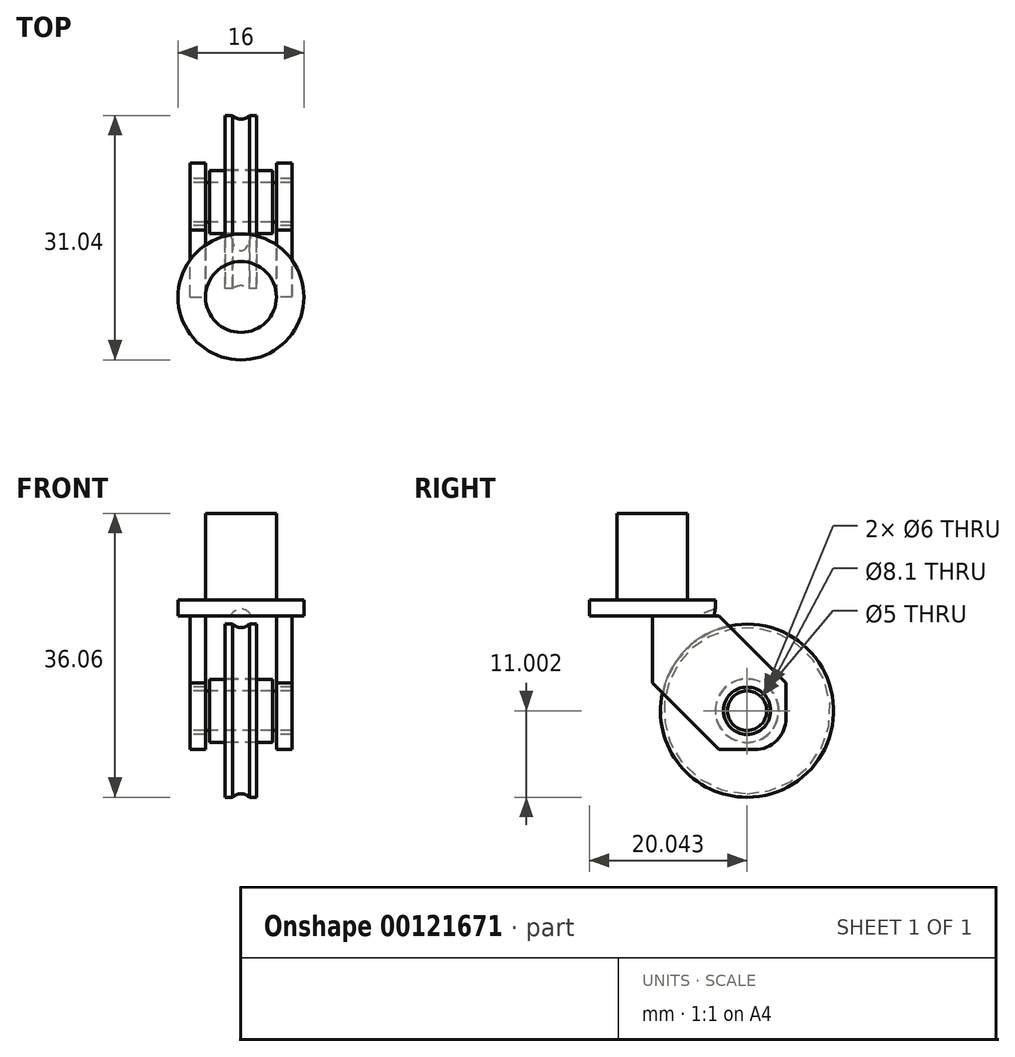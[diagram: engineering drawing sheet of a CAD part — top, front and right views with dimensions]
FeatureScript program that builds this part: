
annotation { "Feature Type Name" : "Feature", "Feature Type Description" : "" }
export const myFeature = defineFeature(function(context is Context, id is Id, definition is map)
    precondition{}
    {
        {
            var Q0;
            Q0=qCreatedBy(makeId("Top.planeOp"),FACE);
            var sketch = newSketch(context, id + "F0", { "sketchPlane" : qUnion([Q0])});
            skCircle(sketch, "E0", {"center": v(0, 0) * mm, "radius": 4.5 * mm});
            skCircle(sketch, "E1", {"center": v(0, 0) * mm, "radius": 8 * mm});
            skLineSegment(sketch, "E2.bottom", {"start": v(-6.5, 0) * mm, "end": v(-4.5, 0) * mm});
            skLineSegment(sketch, "E2.top", {"start": v(-6.5, 17) * mm, "end": v(-4.5, 17) * mm});
            skLineSegment(sketch, "E2.left", {"start": v(-6.5, 0) * mm, "end": v(-6.5, 17) * mm});
            skLineSegment(sketch, "E2.right", {"start": v(-4.5, 0) * mm, "end": v(-4.5, 17) * mm});
            skLineSegment(sketch, "E3.MirrorCS", {"start": v(6.5, 17) * mm, "end": v(4.5, 17) * mm});
            skLineSegment(sketch, "E4.MirrorCS", {"start": v(6.5, 0) * mm, "end": v(4.5, 0) * mm});
            skLineSegment(sketch, "E5.MirrorCS", {"start": v(4.5, 0) * mm, "end": v(4.5, 17) * mm});
            skLineSegment(sketch, "E6.MirrorCS", {"start": v(6.5, 0) * mm, "end": v(6.5, 17) * mm});
            skSolve(sketch);
        }
        {
            var Q0;
            {var subQ0=sQuery(id+"F0.wireOp",EDGE,"E0");var subQ1=makeQuery(id+"F0.imprint","INTERSECT",VERTEX,{"derivedFrom":[subQ0,sQuery(id+"F0.wireOp",EDGE,"E2.bottom"),sQuery(id+"F0.wireOp",EDGE,"E2.right")]});Q0=makeQuery(id+"F0.imprint","IMPRINT",FACE,{"disambiguationData":[TD([[makeQuery(id+"F0.imprint","IMPRINT",EDGE,{"disambiguationData":[TD([[subQ1,1.0]])],"derivedFrom":subQ0}),1.0]])]});}
            extrude(context, id + "F1", {"entities" : qUnion([Q0]), "depth" : 13 * mm});
        }
        {
            var Q0;
            {var subQ3=sQuery(id+"F0.wireOp",EDGE,"E5.MirrorCS");var subQ5=sQuery(id+"F0.wireOp",EDGE,"E1");var subQ6=makeQuery(id+"F0.imprint","INTERSECT",VERTEX,{"derivedFrom":[subQ5,subQ3]});Q0=makeQuery(id+"F0.imprint","IMPRINT",FACE,{"disambiguationData":[TD([[makeQuery(id+"F0.imprint","IMPRINT",EDGE,{"disambiguationData":[TD([[subQ6,-1.0]])],"derivedFrom":subQ5}),1.0]])]});}
            var Q1;
            {var subQ0=sQuery(id+"F0.wireOp",EDGE,"E2.bottom");Q1=makeQuery(id+"F0.imprint","IMPRINT",FACE,{"disambiguationData":[TD([[makeQuery(id+"F0.imprint","IMPRINT",EDGE,{"derivedFrom":subQ0}),1.0]])]});}
            var Q2;
            {var subQ0=sQuery(id+"F0.wireOp",EDGE,"E2.bottom");Q2=makeQuery(id+"F0.imprint","IMPRINT",FACE,{"disambiguationData":[TD([[makeQuery(id+"F0.imprint","IMPRINT",EDGE,{"derivedFrom":subQ0}),-1.0]])]});}
            var Q3;
            {var subQ0=sQuery(id+"F0.wireOp",EDGE,"E4.MirrorCS");Q3=makeQuery(id+"F0.imprint","IMPRINT",FACE,{"disambiguationData":[TD([[makeQuery(id+"F0.imprint","IMPRINT",EDGE,{"derivedFrom":subQ0}),-1.0]])]});}
            extrude(context, id + "F2", {"entities" : qUnion([Q0, Q1, Q2, Q3]), "operationType" : NewBodyOperationType.ADD, "depth" : 2 * mm});
        }
        {
            var Q0;
            {var subQ4=sQuery(id+"F0.wireOp",EDGE,"E2.top");Q0=makeQuery(id+"F0.imprint","IMPRINT",FACE,{"disambiguationData":[TD([[makeQuery(id+"F0.imprint","IMPRINT",EDGE,{"derivedFrom":subQ4}),-1.0]])]});}
            var Q1;
            {var subQ4=sQuery(id+"F0.wireOp",EDGE,"E3.MirrorCS");Q1=makeQuery(id+"F0.imprint","IMPRINT",FACE,{"disambiguationData":[TD([[makeQuery(id+"F0.imprint","IMPRINT",EDGE,{"derivedFrom":subQ4}),1.0]])]});}
            var Q2;
            {var subQ0=sQuery(id+"F0.wireOp",EDGE,"E2.bottom");Q2=makeQuery(id+"F0.imprint","IMPRINT",FACE,{"disambiguationData":[TD([[makeQuery(id+"F0.imprint","IMPRINT",EDGE,{"derivedFrom":subQ0}),1.0]])]});}
            var Q3;
            {var subQ0=sQuery(id+"F0.wireOp",EDGE,"E4.MirrorCS");Q3=makeQuery(id+"F0.imprint","IMPRINT",FACE,{"disambiguationData":[TD([[makeQuery(id+"F0.imprint","IMPRINT",EDGE,{"derivedFrom":subQ0}),-1.0]])]});}
            extrude(context, id + "F3", {"entities" : qUnion([Q0, Q1, Q2, Q3]), "operationType" : NewBodyOperationType.ADD, "oppositeDirection" : true, "depth" : 17 * mm});
        }
        {
            var Q0;
            Q0=makeQuery(id+"F3.opExtrude","SWEPT_FACE",FACE,{"disambiguationData":[OSD([sQuery(id+"F0.wireOp",EDGE,"E2.left")])]});
            var sketch = newSketch(context, id + "F4", { "sketchPlane" : qUnion([Q0])});
            skLineSegment(sketch, "E7", {"start": v(0, -8.5) * mm, "end": v(-8.5, -17) * mm});
            skLineSegment(sketch, "E8", {"start": v(-8.5, 0) * mm, "end": v(-17, -8.5) * mm});
            skPoint(sketch, "E9", {"position": v(-12.04, -12.06) * mm});
            skSolve(sketch);
        }
        {
            var Q0;
            {var subQ0=sQuery(id+"F4.wireOp",EDGE,"E8");Q0=makeQuery(id+"F4.imprint","IMPRINT",FACE,{"disambiguationData":[TD([[makeQuery(id+"F4.imprint","IMPRINT",EDGE,{"derivedFrom":subQ0}),-1.0]])]});}
            var Q1;
            {var subQ0=sQuery(id+"F4.wireOp",EDGE,"E7");Q1=makeQuery(id+"F4.imprint","IMPRINT",FACE,{"disambiguationData":[TD([[makeQuery(id+"F4.imprint","IMPRINT",EDGE,{"derivedFrom":subQ0}),1.0]])]});}
            extrude(context, id + "F5", {"entities" : qUnion([Q0, Q1]), "operationType" : NewBodyOperationType.REMOVE, "oppositeDirection" : true, "depth" : 14 * mm});
        }
        {
            var Q0;
            Q0=makeQuery(id+"F3.opExtrude","CAP_EDGE",EDGE,{"disambiguationData":[OSD([sQuery(id+"F0.wireOp",EDGE,"E2.top")])],"isStart":false});
            var Q1;
            Q1=makeQuery(id+"F3.opExtrude","CAP_EDGE",EDGE,{"disambiguationData":[OSD([sQuery(id+"F0.wireOp",EDGE,"E3.MirrorCS")])],"isStart":false});
            var Q2;
            Q2=makeQuery(id+"F3.opExtrude","CAP_EDGE",EDGE,{"disambiguationData":[OSD([sQuery(id+"F0.wireOp",EDGE,"E2.bottom")])],"isStart":true});
            var Q3;
            Q3=makeQuery(id+"F3.opExtrude","CAP_EDGE",EDGE,{"disambiguationData":[OSD([sQuery(id+"F0.wireOp",EDGE,"E4.MirrorCS")])],"isStart":true});
            var Q4;
            Q4=makeQuery(id+"F5.boolean.opBoolean","COPY",EDGE,{"disambiguationData":[OD(0.0)],"derivedFrom":makeQuery(id+"F5.opExtrude","SWEPT_EDGE",EDGE,{"disambiguationData":[OSD([sQuery(id+"F0.wireOp",EDGE,"E1"),sQuery(id+"F0.wireOp",EDGE,"E2.bottom"),sQuery(id+"F0.wireOp",EDGE,"E2.left"),sQuery(id+"F4.wireOp",EDGE,"E7")])]})});
            var Q5;
            Q5=makeQuery(id+"F5.boolean.opBoolean","COPY",EDGE,{"disambiguationData":[OD(1.0)],"derivedFrom":makeQuery(id+"F5.opExtrude","SWEPT_EDGE",EDGE,{"disambiguationData":[OSD([sQuery(id+"F0.wireOp",EDGE,"E1"),sQuery(id+"F0.wireOp",EDGE,"E2.bottom"),sQuery(id+"F0.wireOp",EDGE,"E2.left"),sQuery(id+"F4.wireOp",EDGE,"E7")])]})});
            var Q6;
            Q6=makeQuery(id+"F5.boolean.opBoolean","COPY",EDGE,{"disambiguationData":[OD(1.0)],"derivedFrom":makeQuery(id+"F5.opExtrude","SWEPT_EDGE",EDGE,{"disambiguationData":[OSD([sQuery(id+"F0.wireOp",EDGE,"E2.left"),sQuery(id+"F4.wireOp",EDGE,"E7")])]})});
            var Q7;
            Q7=makeQuery(id+"F5.boolean.opBoolean","COPY",EDGE,{"disambiguationData":[OD(0.0)],"derivedFrom":makeQuery(id+"F5.opExtrude","SWEPT_EDGE",EDGE,{"disambiguationData":[OSD([sQuery(id+"F0.wireOp",EDGE,"E2.left"),sQuery(id+"F4.wireOp",EDGE,"E7")])]})});
            var Q8;
            Q8=makeQuery(id+"F5.boolean.opBoolean","COPY",EDGE,{"disambiguationData":[OD(0.0)],"derivedFrom":makeQuery(id+"F5.opExtrude","SWEPT_EDGE",EDGE,{"disambiguationData":[OSD([sQuery(id+"F0.wireOp",EDGE,"E2.top"),sQuery(id+"F0.wireOp",EDGE,"E2.left"),sQuery(id+"F4.wireOp",EDGE,"E8")])]})});
            var Q9;
            Q9=makeQuery(id+"F5.boolean.opBoolean","COPY",EDGE,{"disambiguationData":[OD(0.0)],"derivedFrom":makeQuery(id+"F5.opExtrude","SWEPT_EDGE",EDGE,{"disambiguationData":[OSD([sQuery(id+"F0.wireOp",EDGE,"E2.left"),sQuery(id+"F4.wireOp",EDGE,"E8")])]})});
            var Q10;
            Q10=makeQuery(id+"F5.boolean.opBoolean","COPY",EDGE,{"disambiguationData":[OD(1.0)],"derivedFrom":makeQuery(id+"F5.opExtrude","SWEPT_EDGE",EDGE,{"disambiguationData":[OSD([sQuery(id+"F0.wireOp",EDGE,"E2.left"),sQuery(id+"F4.wireOp",EDGE,"E8")])]})});
            var Q11;
            Q11=makeQuery(id+"F5.boolean.opBoolean","COPY",EDGE,{"disambiguationData":[OD(1.0)],"derivedFrom":makeQuery(id+"F5.opExtrude","SWEPT_EDGE",EDGE,{"disambiguationData":[OSD([sQuery(id+"F0.wireOp",EDGE,"E2.top"),sQuery(id+"F0.wireOp",EDGE,"E2.left"),sQuery(id+"F4.wireOp",EDGE,"E8")])]})});
            fillet(context, id + "F6", {"entities" : qUnion([Q0, Q1, Q2, Q3, Q4, Q5, Q6, Q7, Q8, Q9, Q10, Q11]), "radius" : 4 * mm, "tangentPropagation" : true, "allowEdgeOverflow" : false});
        }
        {
            var Q0;
            Q0=sQuery(id+"F4.wireOp",VERTEX,"E9");
            var Q1;
            Q1=makeQuery(id+"F1.opExtrude","SWEPT_BODY",BODY,{"disambiguationData":[OSD([sQuery(id+"F0.wireOp",EDGE,"E0")])]});
            hole(context, id + "F7", {"style" : HoleStyle.SIMPLE, "endStyle" : HoleEndStyle.THROUGH, "holeDiameter" : 6 * mm, "startFromSketch" : true, "locations" : qUnion([Q0]), "scope" : qUnion([Q1]), "isTappedThrough" : true});
        }
        {
            var Q0;
            Q0=qCreatedBy(makeId("Right.planeOp"),FACE);
            var sketch = newSketch(context, id + "F8", { "sketchPlane" : qUnion([Q0])});
            skCircle(sketch, "E10", {"center": v(12.04, -12.06) * mm, "radius": 2.5 * mm});
            skCircle(sketch, "E11", {"center": v(12.04, -12.06) * mm, "radius": 11 * mm});
            skCircle(sketch, "E12", {"center": v(12.04, -12.06) * mm, "radius": 4 * mm});
            skCircle(sketch, "E13", {"center": v(12.04, -12.06) * mm, "radius": 4.05 * mm});
            skSolve(sketch);
        }
        {
            var Q0;
            Q0=makeQuery(id+"F8.imprint","IMPRINT",FACE,{"disambiguationData":[TD([[makeQuery(id+"F8.imprint","IMPRINT",EDGE,{"derivedFrom":sQuery(id+"F8.wireOp",EDGE,"E11")}),1.0]])]});
            extrude(context, id + "F9", {"entities" : qUnion([Q0]), "depth" : 4 * mm, "symmetric" : true});
        }
        {
            var Q0;
            Q0=makeQuery(id+"F8.imprint","IMPRINT",FACE,{"disambiguationData":[TD([[makeQuery(id+"F8.imprint","IMPRINT",EDGE,{"derivedFrom":sQuery(id+"F8.wireOp",EDGE,"E10")}),1.0]])]});
            extrude(context, id + "F10", {"entities" : qUnion([Q0]), "depth" : 13 * mm, "symmetric" : true});
        }
        {
            var Q0;
            Q0=makeQuery(id+"F8.imprint","IMPRINT",FACE,{"disambiguationData":[TD([[makeQuery(id+"F8.imprint","IMPRINT",EDGE,{"derivedFrom":sQuery(id+"F8.wireOp",EDGE,"E10")}),-1.0]])]});
            extrude(context, id + "F11", {"entities" : qUnion([Q0]), "depth" : 8 * mm, "symmetric" : true});
        }
        {
            var Q0;
            Q0=qCreatedBy(makeId("Front.planeOp"),FACE);
            cPlane(context, id + "F12", {"entities" : qUnion([Q0]), "cplaneType" : CPlaneType.OFFSET, "offset" : 11 * mm, "oppositeDirection" : true, "width" : 150 * mm, "height" : 150 * mm});
        }
        {
            var Q0;
            Q0=qCreatedBy(id+"F12.planeOp",FACE);
            var sketch = newSketch(context, id + "F13", { "sketchPlane" : qUnion([Q0])});
            skCircle(sketch, "E14", {"center": v(0, -24.06) * mm, "radius": 1.5 * mm});
            skSolve(sketch);
        }
        {
            var Q0;
            Q0=makeQuery(id+"F13.imprint","IMPRINT",FACE,{"disambiguationData":[TD([[makeQuery(id+"F13.imprint","IMPRINT",EDGE,{"derivedFrom":sQuery(id+"F13.wireOp",EDGE,"E14")}),1.0]])]});
            var Q1;
            Q1=makeQuery(id+"F9.opExtrude","CAP_EDGE",EDGE,{"disambiguationData":[OSD([sQuery(id+"F8.wireOp",EDGE,"E11")])],"isStart":false});
            revolve(context, id + "F14", {"operationType" : NewBodyOperationType.REMOVE, "entities" : qUnion([Q0]), "axis" : qUnion([Q1]), "revolveType" : RevolveType.FULL, "oppositeDirection" : true});
        }
    });
